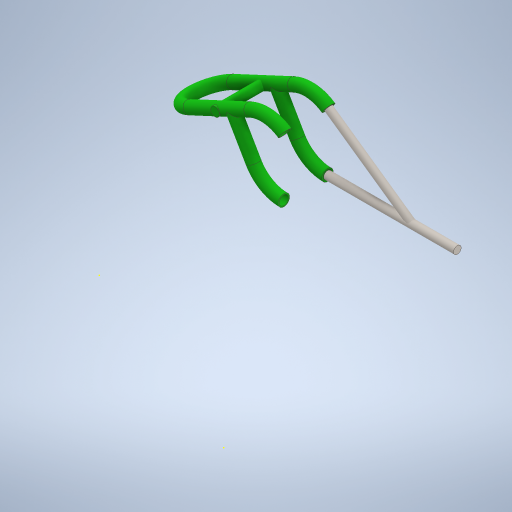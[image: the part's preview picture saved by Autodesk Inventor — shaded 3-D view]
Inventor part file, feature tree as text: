
AUTODESK INVENTOR PART (.ipt)
format: ipt  version: 2024 (Build 280153000, 153)  size: 536,064 bytes
history: native  units: in
note: dims shown in document units (in); Inventor stores cm internally (conversion verified against a paired STEP export)
features: sketch x6, plane x4, extrude x3
ambient origin geometry x8: Origin, YZ Plane, XZ Plane, XY Plane, X Axis, Y Axis, Z Axis, Center Point
bodies: Solid1 (feature_tree), Solid2 (feature_tree), Solid3 (feature_tree), Solid4 (feature_tree), Solid5 (feature_tree), Solid6 (feature_tree), Solid7 (feature_tree), Solid8 (feature_tree), Solid9 (feature_tree), Body1 (feature_tree), Body2 (feature_tree), Body3 (feature_tree), Body4 (feature_tree), Body5 (feature_tree), Body6 (feature_tree), Body7 (feature_tree), Body8 (feature_tree), Body9 (feature_tree)
feature tree (13):
  sketch  "Sketch1"  dims[d0=5.9375in d1=0.0in d2=11.625in d3=0.0in]
  plane  "Work Plane1"
  extrude  "Extrusion1"  Depth=11.625in TaperAngle=0.0deg
  sketch  "Sketch3"  dims[d7=0.1969in d8=0.1969in]
  extrude  "Extrusion2"  Depth=14.875in
  extrude  "Extrusion3"  Depth=0.1969in
  plane  "Work Plane4"
  sketch  "Sketch6"  dims[d11=0.1969in]
  sketch  "Sketch2"  dims[d4=14.875in d5=0.0in d6=1.01in]
  sketch  "Sketch4"  dims[d9=0.1969in]
  sketch  "Sketch5"  dims[d10=0.1969in]
  plane  "Work Plane2"
  plane  "Work Plane3"
